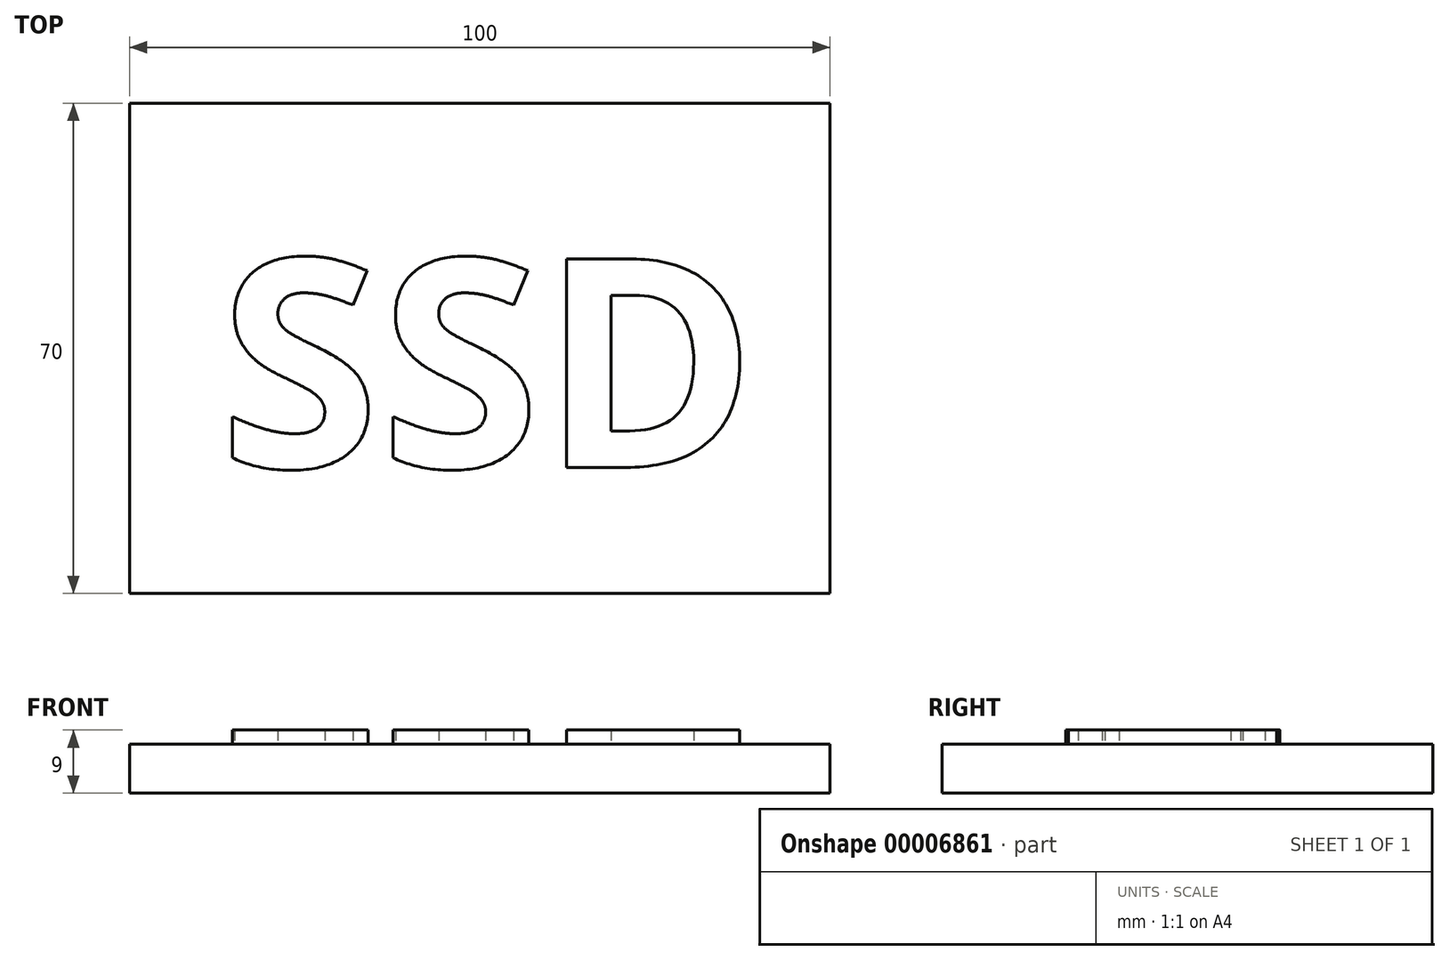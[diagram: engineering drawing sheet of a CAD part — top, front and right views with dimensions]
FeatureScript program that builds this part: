
annotation { "Feature Type Name" : "Feature", "Feature Type Description" : "" }
export const myFeature = defineFeature(function(context is Context, id is Id, definition is map)
    precondition{}
    {
        {
            var Q0;
            Q0=qCreatedBy(makeId("Top.planeOp"),FACE);
            var sketch = newSketch(context, id + "F0", { "sketchPlane" : qUnion([Q0])});
            skLineSegment(sketch, "E0.bottom", {"start": v(-65.33, -4.29) * mm, "end": v(34.67, -4.29) * mm});
            skLineSegment(sketch, "E0.top", {"start": v(-65.33, 65.71) * mm, "end": v(34.67, 65.71) * mm});
            skLineSegment(sketch, "E0.left", {"start": v(-65.33, -4.29) * mm, "end": v(-65.33, 65.71) * mm});
            skLineSegment(sketch, "E0.right", {"start": v(34.67, -4.29) * mm, "end": v(34.67, 65.71) * mm});
            skSolve(sketch);
        }
        {
            var Q0;
            Q0 = qSketchRegion(id + "F0", true);
            extrude(context, id + "F1", {"entities" : qUnion([Q0]), "depth" : 7 * mm});
        }
        {
            var Q0;
            Q0=makeQuery(id+"F1.opExtrude","CAP_FACE",FACE,{"disambiguationData":[OSD([sQuery(id+"F0.wireOp",EDGE,"E0.bottom"),sQuery(id+"F0.wireOp",EDGE,"E0.top"),sQuery(id+"F0.wireOp",EDGE,"E0.left"),sQuery(id+"F0.wireOp",EDGE,"E0.right")])],"isStart":false});
            var sketch = newSketch(context, id + "F2", { "sketchPlane" : qUnion([Q0])});
            skText(sketch, "E1", { "text": "SSD\n", "fontName": "OpenSans-Bold.ttf"});
            const initialGuessF2  = {"E1": [-0.05257, 0.01372, 1, 0, 0.03]};
            skSetInitialGuess(sketch, initialGuessF2);
            skSolve(sketch);
        }
        {
            var Q0;
            Q0 = qSketchRegion(id + "F2", true);
            extrude(context, id + "F3", {"entities" : qUnion([Q0]), "operationType" : NewBodyOperationType.ADD, "depth" : 2 * mm});
        }
    });
